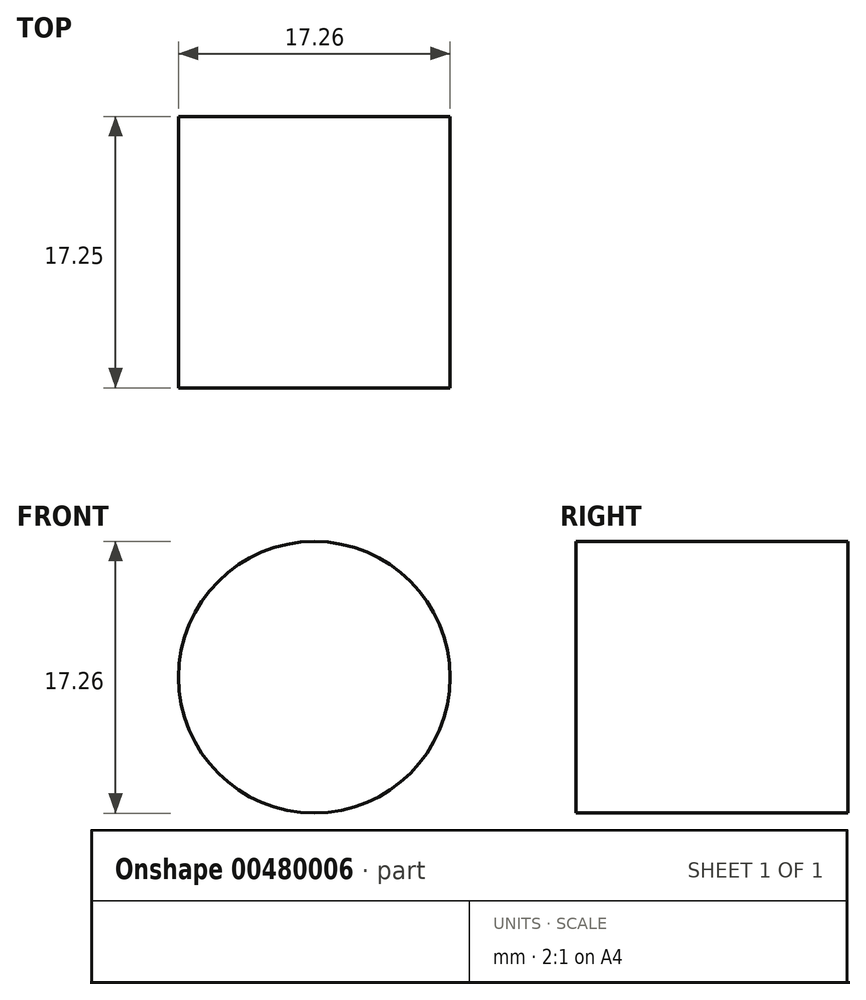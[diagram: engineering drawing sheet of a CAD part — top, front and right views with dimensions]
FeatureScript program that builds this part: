
annotation { "Feature Type Name" : "Feature", "Feature Type Description" : "" }
export const myFeature = defineFeature(function(context is Context, id is Id, definition is map)
    precondition{}
    {
        {
            var Q0;
            Q0=qCreatedBy(makeId("Front.planeOp"),FACE);
            var sketch = newSketch(context, id + "F0", { "sketchPlane" : qUnion([Q0])});
            skCircle(sketch, "E0", {"center": v(0, 0) * mm, "radius": 8.62 * mm});
            skSolve(sketch);
        }
        {
            var Q0;
            Q0=makeQuery(id+"F0.imprint","IMPRINT",FACE,{"disambiguationData":[TD([[makeQuery(id+"F0.imprint","IMPRINT",EDGE,{"derivedFrom":sQuery(id+"F0.wireOp",EDGE,"E0")}),1.0]])]});
            extrude(context, id + "F1", {"entities" : qUnion([Q0]), "depth" : 17.25 * mm});
        }
    });
